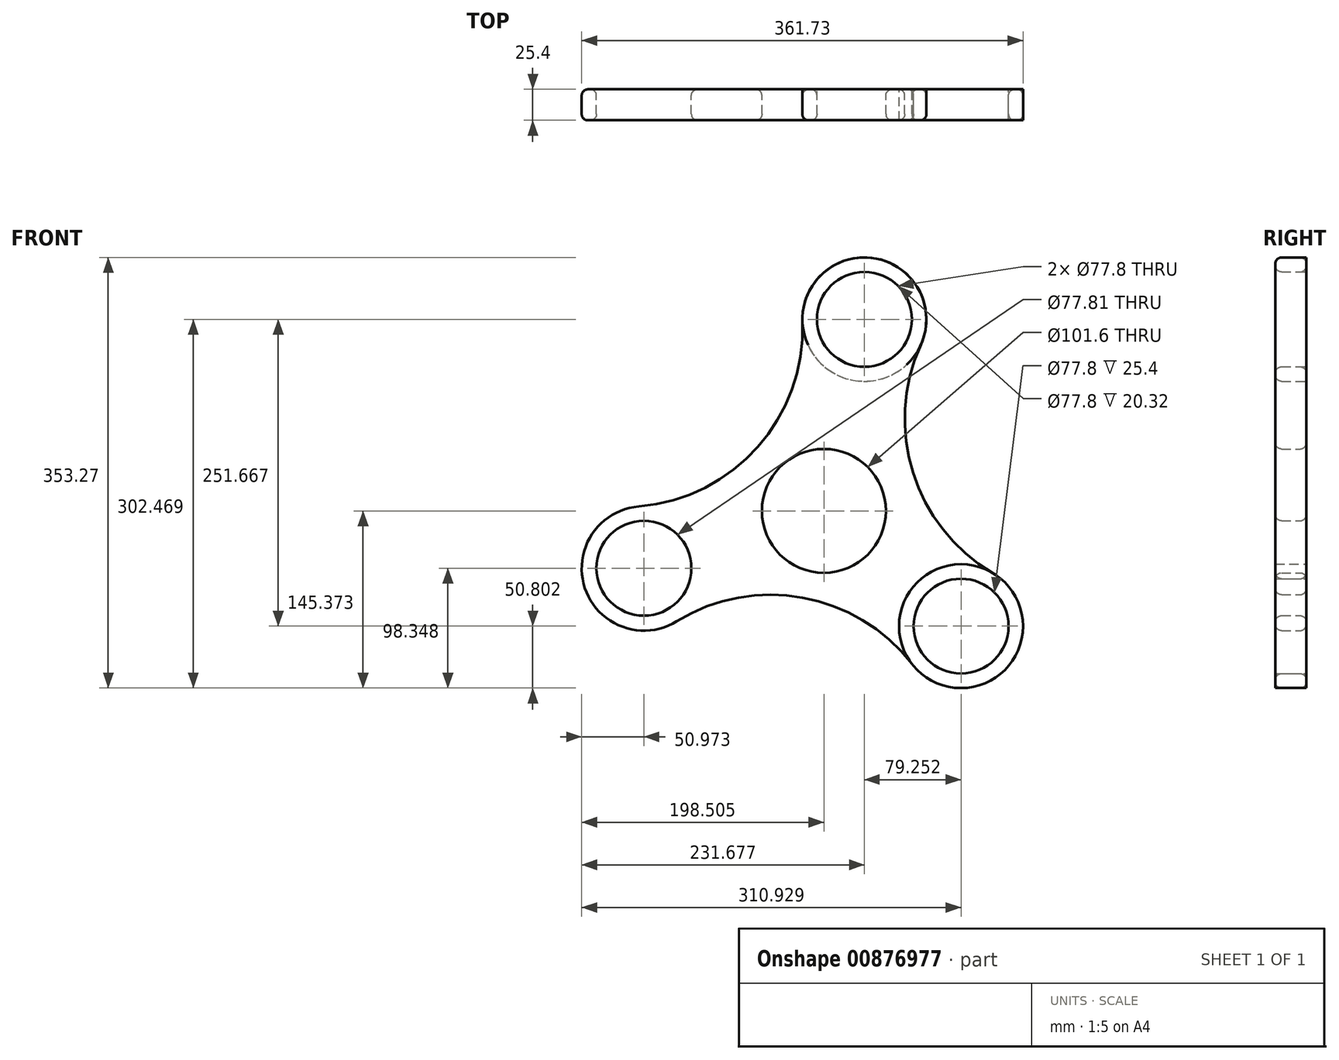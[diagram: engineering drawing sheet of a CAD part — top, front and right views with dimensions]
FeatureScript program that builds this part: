
annotation { "Feature Type Name" : "Feature", "Feature Type Description" : "" }
export const myFeature = defineFeature(function(context is Context, id is Id, definition is map)
    precondition{}
    {
        {
            var Q0;
            Q0=qCreatedBy(makeId("Front.planeOp"),FACE);
            var sketch = newSketch(context, id + "F0", { "sketchPlane" : qUnion([Q0])});
            skCircle(sketch, "E0", {"center": v(120.1, -117.93) * mm, "radius": 50.8 * mm});
            skCircle(sketch, "E1", {"center": v(40.85, 133.74) * mm, "radius": 50.8 * mm});
            skCircle(sketch, "E2", {"center": v(40.85, 133.74) * mm, "radius": 38.9 * mm});
            skCircle(sketch, "E3", {"center": v(120.1, -117.93) * mm, "radius": 38.9 * mm});
            skCircle(sketch, "E4", {"center": v(-139.83, -70.59) * mm, "radius": 51 * mm});
            skCircle(sketch, "E5", {"center": v(-139.86, -70.38) * mm, "radius": 38.9 * mm});
            skArc(sketch, "E6", {"start": v(87.09, 112.7) * mm, "mid": v(80.7, 7.98) * mm, "end": v(145.94, -74.2) * mm});
            skArc(sketch, "E7", {"start": v(-144.1, -19.77) * mm, "mid": v(-46.64, 29.15) * mm, "end": v(-9.92, 131.83) * mm});
            skArc(sketch, "E8", {"start": v(79.92, -149.01) * mm, "mid": v(-9.84, -94.48) * mm, "end": v(-113.03, -113.98) * mm});
            skCircle(sketch, "E9", {"center": v(7.67, -23.36) * mm, "radius": 50.8 * mm});
            skCircle(sketch, "E10", {"center": v(7.67, -23.36) * mm, "radius": 38.9 * mm});
            skSolve(sketch);
        }
        {
            var Q0;
            Q0=makeQuery(id+"F0.imprint","IMPRINT",FACE,{"disambiguationData":[TD([[makeQuery(id+"F0.imprint","IMPRINT",EDGE,{"derivedFrom":sQuery(id+"F0.wireOp",EDGE,"E1")}),1.0]])]});
            var Q1;
            Q1=makeQuery(id+"F0.imprint","IMPRINT",FACE,{"disambiguationData":[TD([[makeQuery(id+"F0.imprint","IMPRINT",EDGE,{"derivedFrom":sQuery(id+"F0.wireOp",EDGE,"E0")}),1.0]])]});
            var Q2;
            Q2=makeQuery(id+"F0.imprint","IMPRINT",FACE,{"disambiguationData":[TD([[makeQuery(id+"F0.imprint","IMPRINT",EDGE,{"derivedFrom":sQuery(id+"F0.wireOp",EDGE,"9Q5FooUE-TwPu-gxHe-aquz-T4JrgoIZ5zyM")}),1.0]])]});
            extrude(context, id + "F1", {"entities" : qUnion([Q0, Q1, Q2]), "depth" : 25.4 * mm, "offsetDistance" : 25.4 * mm});
        }
        {
            var Q0;
            Q0=makeQuery(id+"F1.opExtrude","CAP_FACE",FACE,{"disambiguationData":[OSD([sQuery(id+"F0.wireOp",EDGE,"E1")])],"isStart":false});
            var sketch = newSketch(context, id + "F2", { "sketchPlane" : qUnion([Q0])});
            skCircle(sketch, "E11", {"center": v(40.85, 133.74) * mm, "radius": 36.05 * mm});
            skSolve(sketch);
        }
        {
            var Q0;
            Q0=makeQuery(id+"F2.imprint","IMPRINT",FACE,{"disambiguationData":[TD([[makeQuery(id+"F2.imprint","IMPRINT",EDGE,{"derivedFrom":sQuery(id+"F2.wireOp",EDGE,"E11")}),1.0]])]});
            extrude(context, id + "F3", {"entities" : qUnion([Q0]), "operationType" : NewBodyOperationType.REMOVE, "oppositeDirection" : true, "depth" : 25.4 * mm, "offsetDistance" : 25.4 * mm});
        }
        {
            var Q0;
            Q0 = qSketchRegion(id + "F0", true);
            extrude(context, id + "F4", {"entities" : qUnion([Q0]), "depth" : 25.4 * mm, "offsetDistance" : 25.4 * mm});
        }
        {
            var Q0;
            Q0=makeQuery(id+"F1.opExtrude","CAP_FACE",FACE,{"disambiguationData":[OSD([sQuery(id+"F0.wireOp",EDGE,"E1"),sQuery(id+"F0.wireOp",EDGE,"E2")])],"isStart":false});
            var Q1;
            Q1=makeQuery(id+"F4.opExtrude","CAP_FACE",FACE,{"disambiguationData":[OSD([sQuery(id+"F0.wireOp",EDGE,"E0"),sQuery(id+"F0.wireOp",EDGE,"E1"),sQuery(id+"F0.wireOp",EDGE,"E2"),sQuery(id+"F0.wireOp",EDGE,"E3"),sQuery(id+"F0.wireOp",EDGE,"E4"),sQuery(id+"F0.wireOp",EDGE,"E5"),sQuery(id+"F0.wireOp",EDGE,"E6"),sQuery(id+"F0.wireOp",EDGE,"E7"),sQuery(id+"F0.wireOp",EDGE,"E8"),sQuery(id+"F0.wireOp",EDGE,"E9")])],"isStart":true});
            var Q2;
            Q2=makeQuery(id+"F4.opExtrude","CAP_FACE",FACE,{"disambiguationData":[OSD([sQuery(id+"F0.wireOp",EDGE,"E0"),sQuery(id+"F0.wireOp",EDGE,"E1"),sQuery(id+"F0.wireOp",EDGE,"E2"),sQuery(id+"F0.wireOp",EDGE,"E3"),sQuery(id+"F0.wireOp",EDGE,"E4"),sQuery(id+"F0.wireOp",EDGE,"E5"),sQuery(id+"F0.wireOp",EDGE,"E6"),sQuery(id+"F0.wireOp",EDGE,"E7"),sQuery(id+"F0.wireOp",EDGE,"E8"),sQuery(id+"F0.wireOp",EDGE,"E9")])],"isStart":false});
            var Q3;
            Q3=makeQuery(id+"F4.opExtrude","SWEPT_FACE",FACE,{"disambiguationData":[OSD([sQuery(id+"F0.wireOp",EDGE,"E7")])]});
            fillet(context, id + "F5", {"entities" : qUnion([Q0, Q1, Q2, Q3]), "radius" : 5.08 * mm, "tangentPropagation" : true, "allowEdgeOverflow" : false});
        }
    });
